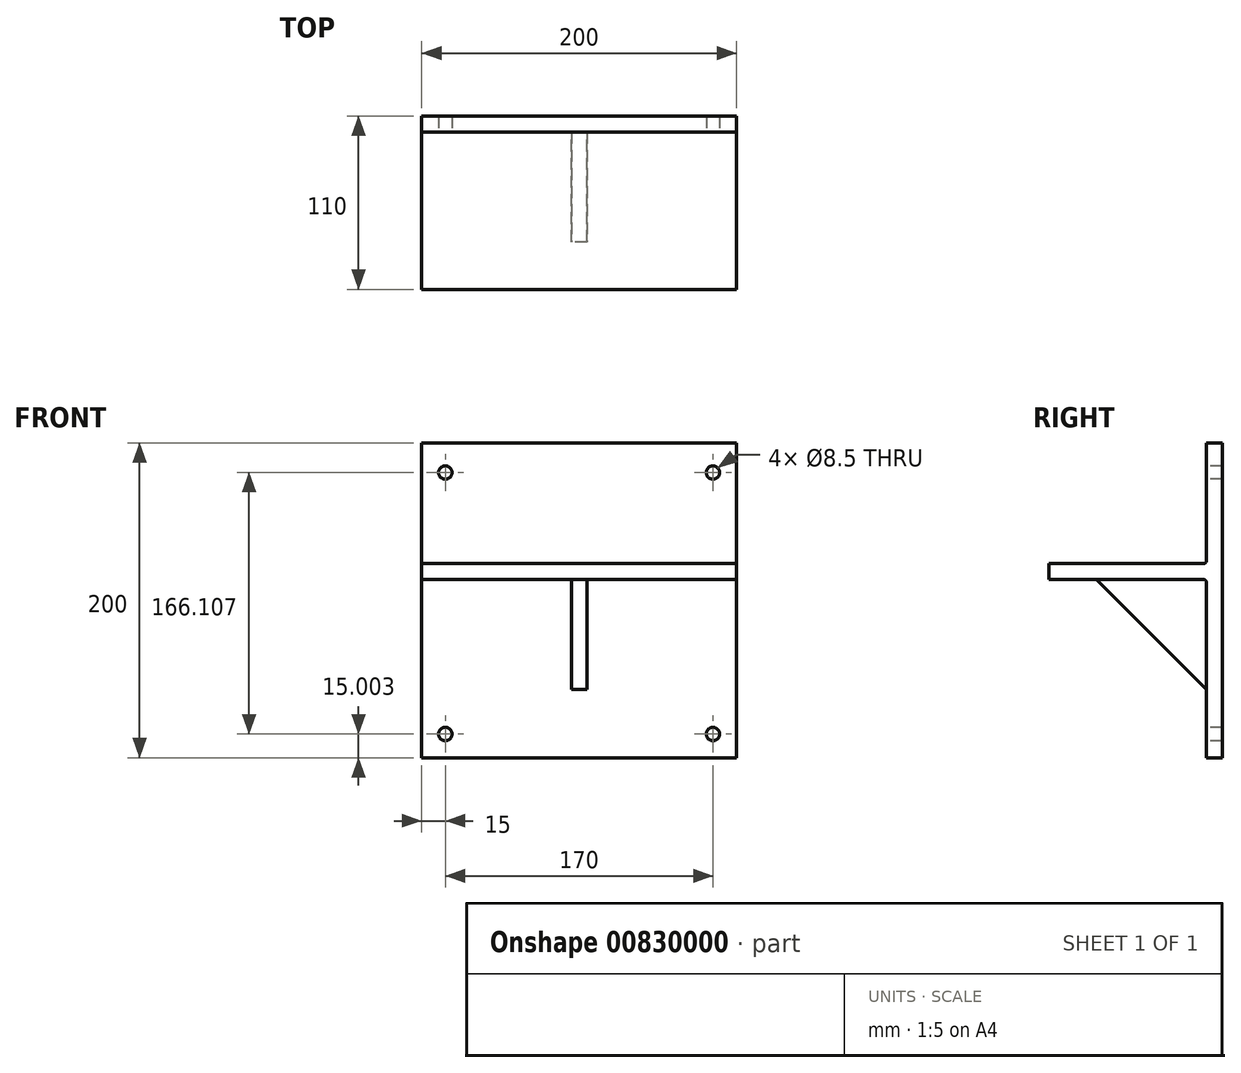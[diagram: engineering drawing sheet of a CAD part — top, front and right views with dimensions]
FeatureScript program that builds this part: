
annotation { "Feature Type Name" : "Feature", "Feature Type Description" : "" }
export const myFeature = defineFeature(function(context is Context, id is Id, definition is map)
    precondition{}
    {
        {
            var Q0;
            Q0=qCreatedBy(makeId("Right.planeOp"),FACE);
            var sketch = newSketch(context, id + "F0", { "sketchPlane" : qUnion([Q0])});
            skLineSegment(sketch, "E0.bottom", {"start": v(-24.83, 18.9) * mm, "end": v(-34.83, 18.9) * mm});
            skLineSegment(sketch, "E0.top", {"start": v(-24.83, -181.1) * mm, "end": v(-34.83, -181.1) * mm});
            skLineSegment(sketch, "E0.left", {"start": v(-24.83, 18.9) * mm, "end": v(-24.83, -181.1) * mm});
            skLineSegment(sketch, "E0.right", {"start": v(-34.83, 18.9) * mm, "end": v(-34.83, -181.1) * mm});
            skLineSegment(sketch, "E1.bottom", {"start": v(-34.83, -57.9) * mm, "end": v(-134.83, -57.9) * mm});
            skLineSegment(sketch, "E1.top", {"start": v(-34.83, -67.9) * mm, "end": v(-134.83, -67.9) * mm});
            skLineSegment(sketch, "E1.left", {"start": v(-34.83, -57.9) * mm, "end": v(-34.83, -67.9) * mm});
            skLineSegment(sketch, "E1.right", {"start": v(-134.83, -57.9) * mm, "end": v(-134.83, -67.9) * mm});
            skSolve(sketch);
        }
        {
            var Q0;
            Q0 = qSketchRegion(id + "F0", true);
            extrude(context, id + "F1", {"entities" : qUnion([Q0]), "depth" : 25 * mm, "offsetDistance" : 25 * mm});
        }
        {
            var Q0;
            Q0 = qSketchRegion(id + "F0", true);
            var Q1;
            Q1=makeQuery(id+"F1.opExtrude","CAP_FACE",FACE,{"disambiguationData":[OSD([sQuery(id+"F0.wireOp",EDGE,"E0.bottom"),sQuery(id+"F0.wireOp",EDGE,"E0.top"),sQuery(id+"F0.wireOp",EDGE,"E0.left"),sQuery(id+"F0.wireOp",EDGE,"E0.right"),sQuery(id+"F0.wireOp",EDGE,"E1.bottom"),sQuery(id+"F0.wireOp",EDGE,"E1.top"),sQuery(id+"F0.wireOp",EDGE,"E1.right")])],"isStart":true});
            extrude(context, id + "F2", {"entities" : qUnion([Q0, Q1]), "operationType" : NewBodyOperationType.ADD, "depth" : 200 * mm, "offsetDistance" : 25 * mm});
        }
        {
            var Q0;
            {var subQ0=sQuery(id+"F0.wireOp",EDGE,"E0.right");var subQ1=makeQuery(id+"F0.imprint","IMPRINT",EDGE,{"disambiguationData":[TD([[makeQuery(id+"F0.imprint","INTERSECT",VERTEX,{"derivedFrom":[sQuery(id+"F0.wireOp",EDGE,"E0.bottom"),subQ0]}),-1.0]])],"derivedFrom":subQ0});Q0=makeQuery(id+"F2.boolean.opBoolean","MERGE",FACE,{"derivedFrom":[makeQuery(id+"F1.opExtrude","SWEPT_FACE",FACE,{"disambiguationData":[OSD([subQ0]),TDD([subQ1])]}),makeQuery(id+"F2.opExtrude","SWEPT_FACE",FACE,{"disambiguationData":[OSD([subQ0]),TDD([subQ1])]})]});}
            var sketch = newSketch(context, id + "F3", { "sketchPlane" : qUnion([Q0])});
            skPoint(sketch, "E2", {"position": v(15, 0) * mm});
            skPoint(sketch, "E3", {"position": v(185, 0) * mm});
            skPoint(sketch, "E4", {"position": v(185, -166.1) * mm});
            skPoint(sketch, "E5", {"position": v(15, -166.1) * mm});
            skSolve(sketch);
        }
        {
            var Q0;
            Q0=sQuery(id+"F3.wireOp",VERTEX,"E2");
            var Q1;
            Q1=sQuery(id+"F3.wireOp",VERTEX,"E3");
            var Q2;
            Q2=sQuery(id+"F3.wireOp",VERTEX,"E4");
            var Q3;
            Q3=sQuery(id+"F3.wireOp",VERTEX,"E5");
            var Q4;
            Q4=makeQuery(id+"F1.opExtrude","SWEPT_BODY",BODY,{"disambiguationData":[OSD([sQuery(id+"F0.wireOp",EDGE,"E0.bottom"),sQuery(id+"F0.wireOp",EDGE,"E0.top"),sQuery(id+"F0.wireOp",EDGE,"E0.left"),sQuery(id+"F0.wireOp",EDGE,"E0.right"),sQuery(id+"F0.wireOp",EDGE,"E1.bottom"),sQuery(id+"F0.wireOp",EDGE,"E1.top"),sQuery(id+"F0.wireOp",EDGE,"E1.right")])]});
            hole(context, id + "F4", {"style" : HoleStyle.SIMPLE, "endStyle" : HoleEndStyle.THROUGH, "holeDiameter" : 8.5 * mm, "majorDiameter" : 5 * mm, "isTappedThrough" : true, "tappedDepth" : 12 * mm, "tapClearance" : 3, "locations" : qUnion([Q0, Q1, Q2, Q3]), "scope" : qUnion([Q4])});
        }
        {
            var Q0;
            {var subQ0=sQuery(id+"F0.wireOp",EDGE,"E0.right");var subQ1=makeQuery(id+"F0.imprint","IMPRINT",EDGE,{"disambiguationData":[TD([[makeQuery(id+"F0.imprint","INTERSECT",VERTEX,{"derivedFrom":[sQuery(id+"F0.wireOp",EDGE,"E0.top"),subQ0]}),1.0]])],"derivedFrom":subQ0});Q0=makeQuery(id+"F2.boolean.opBoolean","MERGE",FACE,{"derivedFrom":[makeQuery(id+"F1.opExtrude","SWEPT_FACE",FACE,{"disambiguationData":[OSD([subQ0]),TDD([subQ1])]}),makeQuery(id+"F2.opExtrude","SWEPT_FACE",FACE,{"disambiguationData":[OSD([subQ0]),TDD([subQ1])]})]});}
            var sketch = newSketch(context, id + "F5", { "sketchPlane" : qUnion([Q0])});
            skLineSegment(sketch, "E6.bottom", {"start": v(95, -67.9) * mm, "end": v(105, -67.9) * mm});
            skLineSegment(sketch, "E6.top", {"start": v(95, -137.9) * mm, "end": v(105, -137.9) * mm});
            skLineSegment(sketch, "E6.left", {"start": v(95, -67.9) * mm, "end": v(95, -137.9) * mm});
            skLineSegment(sketch, "E6.right", {"start": v(105, -67.9) * mm, "end": v(105, -137.9) * mm});
            skSolve(sketch);
        }
        {
            var Q0;
            Q0=makeQuery(id+"F5.imprint","IMPRINT",FACE,{"disambiguationData":[TD([[makeQuery(id+"F5.imprint","IMPRINT",EDGE,{"derivedFrom":sQuery(id+"F5.wireOp",EDGE,"E6.bottom")}),1.0]])]});
            extrude(context, id + "F6", {"entities" : qUnion([Q0]), "operationType" : NewBodyOperationType.ADD, "depth" : 70 * mm, "offsetDistance" : 25 * mm});
        }
        {
            var Q0;
            Q0=makeQuery(id+"F6.opExtrude","SWEPT_FACE",FACE,{"disambiguationData":[OSD([sQuery(id+"F5.wireOp",EDGE,"E6.left")])]});
            var sketch = newSketch(context, id + "F7", { "sketchPlane" : qUnion([Q0])});
            skLineSegment(sketch, "E7", {"start": v(34.83, -137.9) * mm, "end": v(104.83, -67.9) * mm});
            skSolve(sketch);
        }
        {
            var Q0;
            Q0=makeQuery(id+"F7.imprint","IMPRINT",FACE,{"disambiguationData":[TD([[makeQuery(id+"F7.imprint","IMPRINT",EDGE,{"derivedFrom":sQuery(id+"F7.wireOp",EDGE,"E7")}),-1.0]])]});
            extrude(context, id + "F8", {"entities" : qUnion([Q0]), "operationType" : NewBodyOperationType.REMOVE, "oppositeDirection" : true, "depth" : 10 * mm, "offsetDistance" : 25 * mm});
        }
        {
            var Q0;
            {var subQ0=sQuery(id+"F0.wireOp",EDGE,"E1.left");var subQ1=sQuery(id+"F0.wireOp",EDGE,"E1.bottom");var subQ2=sQuery(id+"F0.wireOp",EDGE,"E0.right");Q0=makeQuery(id+"F2.boolean.opBoolean","MERGE",EDGE,{"derivedFrom":[makeQuery(id+"F1.opExtrude","SWEPT_EDGE",EDGE,{"disambiguationData":[OSD([subQ2,subQ1,subQ0])]}),makeQuery(id+"F2.opExtrude","SWEPT_EDGE",EDGE,{"disambiguationData":[OSD([subQ2,subQ1,subQ0]),TDD([makeQuery(id+"F0.imprint","INTERSECT",VERTEX,{"derivedFrom":[subQ2,subQ1,subQ0]})])]})]});}
            var Q1;
            {var subQ0=sQuery(id+"F0.wireOp",EDGE,"E0.right");var subQ2=sQuery(id+"F0.wireOp",EDGE,"E1.left");var subQ3=sQuery(id+"F0.wireOp",EDGE,"E1.top");var subQ4=makeQuery(id+"F0.imprint","INTERSECT",VERTEX,{"derivedFrom":[subQ0,subQ3,subQ2]});Q1=makeQuery(id+"F6.boolean.opBoolean","SPLIT",EDGE,{"disambiguationData":[TD([makeQuery(id+"F6.opExtrude","SWEPT_FACE",FACE,{"disambiguationData":[OSD([sQuery(id+"F5.wireOp",EDGE,"E6.left")])]})])],"derivedFrom":makeQuery(id+"F2.boolean.opBoolean","MERGE",EDGE,{"derivedFrom":[makeQuery(id+"F1.opExtrude","SWEPT_EDGE",EDGE,{"disambiguationData":[OSD([subQ0,subQ3,subQ2])]}),makeQuery(id+"F2.opExtrude","SWEPT_EDGE",EDGE,{"disambiguationData":[OSD([subQ0,subQ3,subQ2]),TDD([subQ4])]})]})});}
            var Q2;
            {var subQ0=sQuery(id+"F0.wireOp",EDGE,"E0.right");var subQ2=sQuery(id+"F0.wireOp",EDGE,"E1.left");var subQ3=sQuery(id+"F0.wireOp",EDGE,"E1.top");var subQ4=makeQuery(id+"F0.imprint","INTERSECT",VERTEX,{"derivedFrom":[subQ0,subQ3,subQ2]});Q2=makeQuery(id+"F6.boolean.opBoolean","SPLIT",EDGE,{"disambiguationData":[TD([makeQuery(id+"F6.opExtrude","SWEPT_FACE",FACE,{"disambiguationData":[OSD([sQuery(id+"F5.wireOp",EDGE,"E6.right")])]})])],"derivedFrom":makeQuery(id+"F2.boolean.opBoolean","MERGE",EDGE,{"derivedFrom":[makeQuery(id+"F1.opExtrude","SWEPT_EDGE",EDGE,{"disambiguationData":[OSD([subQ0,subQ3,subQ2])]}),makeQuery(id+"F2.opExtrude","SWEPT_EDGE",EDGE,{"disambiguationData":[OSD([subQ0,subQ3,subQ2]),TDD([subQ4])]})]})});}
            var Q3;
            Q3=makeQuery(id+"F6.opExtrude","CAP_EDGE",EDGE,{"disambiguationData":[OSD([sQuery(id+"F5.wireOp",EDGE,"E6.left")])],"isStart":true});
            var Q4;
            Q4=makeQuery(id+"F6.opExtrude","SWEPT_EDGE",EDGE,{"disambiguationData":[OSD([sQuery(id+"F0.wireOp",EDGE,"E0.right"),sQuery(id+"F0.wireOp",EDGE,"E1.top"),sQuery(id+"F0.wireOp",EDGE,"E1.left"),sQuery(id+"F5.wireOp",EDGE,"E6.bottom"),sQuery(id+"F5.wireOp",EDGE,"E6.left")])]});
            var Q5;
            {var subQ0=sQuery(id+"F5.wireOp",EDGE,"E6.top");Q5=makeQuery(id+"F8.boolean.opBoolean","MERGE",EDGE,{"derivedFrom":[makeQuery(id+"F6.opExtrude","CAP_EDGE",EDGE,{"disambiguationData":[OSD([subQ0])],"isStart":true}),makeQuery(id+"F8.opExtrude","SWEPT_EDGE",EDGE,{"disambiguationData":[OSD([subQ0,sQuery(id+"F5.wireOp",EDGE,"E6.left"),sQuery(id+"F7.wireOp",EDGE,"E7")])]})]});}
            var Q6;
            {var subQ0=sQuery(id+"F5.wireOp",EDGE,"E6.bottom");Q6=makeQuery(id+"F8.boolean.opBoolean","MERGE",EDGE,{"derivedFrom":[makeQuery(id+"F6.opExtrude","CAP_EDGE",EDGE,{"disambiguationData":[OSD([subQ0])],"isStart":false}),makeQuery(id+"F8.opExtrude","SWEPT_EDGE",EDGE,{"disambiguationData":[OSD([sQuery(id+"F0.wireOp",EDGE,"E0.right"),sQuery(id+"F0.wireOp",EDGE,"E1.top"),sQuery(id+"F0.wireOp",EDGE,"E1.left"),subQ0,sQuery(id+"F5.wireOp",EDGE,"E6.left"),sQuery(id+"F7.wireOp",EDGE,"E7")])]})]});}
            var Q7;
            Q7=makeQuery(id+"F6.opExtrude","CAP_EDGE",EDGE,{"disambiguationData":[OSD([sQuery(id+"F5.wireOp",EDGE,"E6.right")])],"isStart":true});
            var Q8;
            Q8=makeQuery(id+"F6.opExtrude","SWEPT_EDGE",EDGE,{"disambiguationData":[OSD([sQuery(id+"F0.wireOp",EDGE,"E0.right"),sQuery(id+"F0.wireOp",EDGE,"E1.top"),sQuery(id+"F0.wireOp",EDGE,"E1.left"),sQuery(id+"F5.wireOp",EDGE,"E6.bottom"),sQuery(id+"F5.wireOp",EDGE,"E6.right")])]});
            fillet(context, id + "F9", {"entities" : qUnion([Q0, Q1, Q2, Q3, Q4, Q5, Q6, Q7, Q8]), "radius" : 2 * mm, "tangentPropagation" : true, "allowEdgeOverflow" : false});
        }
    });
